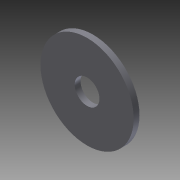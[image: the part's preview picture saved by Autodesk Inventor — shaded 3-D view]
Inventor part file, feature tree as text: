
AUTODESK INVENTOR PART (.ipt)
format: ipt  version: 2014 SP1 (Build 180222100, 222)  size: 76,288 bytes
history: native  units: in
note: dims shown in document units (in); Inventor stores cm internally (conversion verified against a paired STEP export)
features: extrude x1, sketch x1
ambient origin geometry x8: Origin, YZ Plane, XZ Plane, XY Plane, X Axis, Y Axis, Z Axis, Center Point
bodies: Solid1 (feature_tree)
feature tree (2):
  extrude  "Extrusion1"  Depth=0.0625in
  sketch  "Sketch1"  dims[d0=0.266in d1=1.0in d2=0.0625in d3=0.0in]
